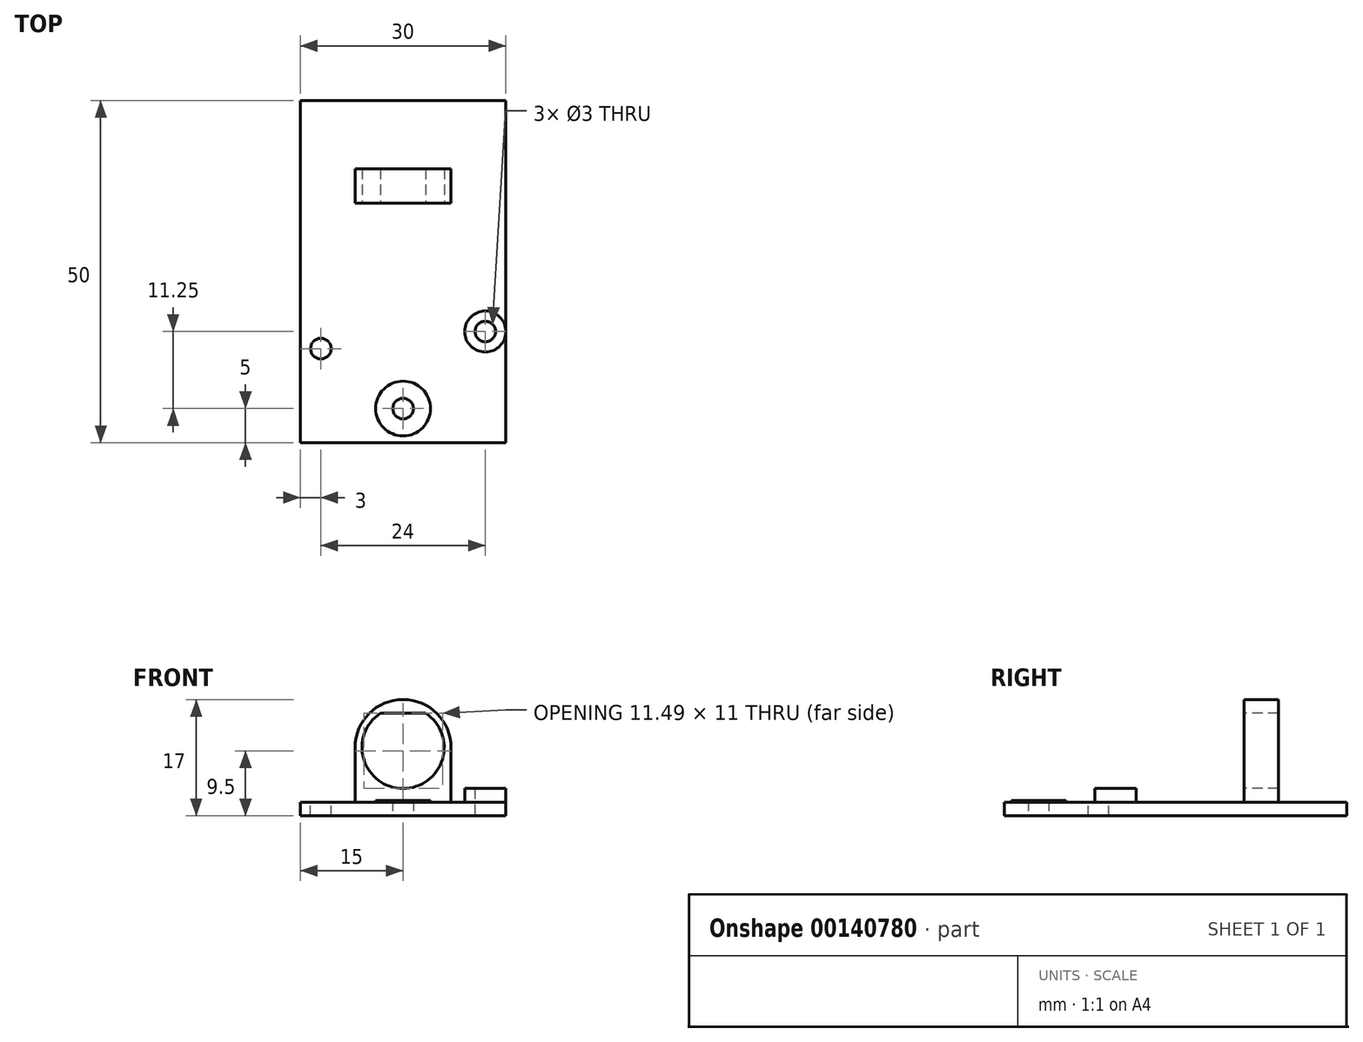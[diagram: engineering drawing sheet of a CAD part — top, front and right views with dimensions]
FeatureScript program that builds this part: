
annotation { "Feature Type Name" : "Feature", "Feature Type Description" : "" }
export const myFeature = defineFeature(function(context is Context, id is Id, definition is map)
    precondition{}
    {
        {
            var Q0;
            Q0=qCreatedBy(makeId("Front.planeOp"),FACE);
            var sketch = newSketch(context, id + "F0", { "sketchPlane" : qUnion([Q0])});
            skLineSegment(sketch, "E0.bottom", {"start": v(-3.32, 15) * mm, "end": v(3.32, 15) * mm});
            skArc(sketch, "E1", {"start": v(7, 10) * mm, "mid": v(0, 17) * mm, "end": v(-7, 10) * mm});
            skLineSegment(sketch, "E2", {"start": v(-7, 10) * mm, "end": v(-7, 2) * mm});
            skLineSegment(sketch, "E3", {"start": v(7, 10) * mm, "end": v(7, 2) * mm});
            skLineSegment(sketch, "E4", {"start": v(-7, 2) * mm, "end": v(-15, 2) * mm});
            skLineSegment(sketch, "E5", {"start": v(-15, 2) * mm, "end": v(-15, 0) * mm});
            skLineSegment(sketch, "E6", {"start": v(15, 0) * mm, "end": v(15, 2) * mm});
            skLineSegment(sketch, "E7", {"start": v(15, 2) * mm, "end": v(7, 2) * mm});
            skLineSegment(sketch, "E8", {"start": v(-15, 0) * mm, "end": v(15, 0) * mm});
            skArc(sketch, "E9", {"start": v(-3.32, 15) * mm, "mid": v(0, 4) * mm, "end": v(3.32, 15) * mm});
            skLineSegment(sketch, "E10", {"start": v(-7, 2) * mm, "end": v(7, 2) * mm});
            skSolve(sketch);
        }
        {
            var Q0;
            Q0=makeQuery(id+"F0.imprint","IMPRINT",FACE,{"disambiguationData":[TD([[makeQuery(id+"F0.imprint","IMPRINT",EDGE,{"derivedFrom":sQuery(id+"F0.wireOp",EDGE,"E0.bottom")}),1.0]])]});
            extrude(context, id + "F1", {"entities" : qUnion([Q0]), "oppositeDirection" : true, "depth" : 5 * mm});
        }
        {
            var Q0;
            {var subQ0=sQuery(id+"F0.wireOp",EDGE,"rBDJkf6V-3IXR-hIOR-VNlQ-4rZEFsfYJzs1");Q0=makeQuery(id+"F0.imprint","IMPRINT",FACE,{"disambiguationData":[TD([[makeQuery(id+"F0.imprint","IMPRINT",EDGE,{"derivedFrom":subQ0}),1.0]])]});}
            var Q1;
            {var subQ3=sQuery(id+"F0.wireOp",EDGE,"E4");Q1=makeQuery(id+"F0.imprint","IMPRINT",FACE,{"disambiguationData":[TD([[makeQuery(id+"F0.imprint","IMPRINT",EDGE,{"derivedFrom":subQ3}),1.0]])]});}
            extrude(context, id + "F2", {"entities" : qUnion([Q0, Q1]), "operationType" : NewBodyOperationType.ADD, "oppositeDirection" : true, "depth" : 15 * mm});
        }
        {
            var Q0;
            {var subQ0=sQuery(id+"F0.wireOp",EDGE,"rBDJkf6V-3IXR-hIOR-VNlQ-4rZEFsfYJzs1");Q0=makeQuery(id+"F0.imprint","IMPRINT",FACE,{"disambiguationData":[TD([[makeQuery(id+"F0.imprint","IMPRINT",EDGE,{"derivedFrom":subQ0}),1.0]])]});}
            var Q1;
            {var subQ3=sQuery(id+"F0.wireOp",EDGE,"E4");Q1=makeQuery(id+"F0.imprint","IMPRINT",FACE,{"disambiguationData":[TD([[makeQuery(id+"F0.imprint","IMPRINT",EDGE,{"derivedFrom":subQ3}),1.0]])]});}
            extrude(context, id + "F3", {"entities" : qUnion([Q0, Q1]), "operationType" : NewBodyOperationType.ADD, "depth" : 35 * mm});
        }
        {
            var Q0;
            {var subQ0=sQuery(id+"F0.wireOp",EDGE,"9Bnnmyrw-iAOv-QSIy-XyIa-5J96ybDtpeLF");var subQ1=sQuery(id+"F0.wireOp",EDGE,"OCGj93Nr-ASNq-xmZx-sLMK-JFpCvM9ZKUq5");var subQ2=sQuery(id+"F0.wireOp",EDGE,"E7");var subQ3=sQuery(id+"F0.wireOp",EDGE,"E4");var subQ4=sQuery(id+"F0.wireOp",EDGE,"E0.top");Q0=makeQuery(id+"F3.boolean.opBoolean","MERGE",FACE,{"derivedFrom":[makeQuery(id+"F2.opExtrude","SWEPT_FACE",FACE,{"disambiguationData":[OSD([subQ4,subQ3,subQ2,subQ1,subQ0])]}),makeQuery(id+"F3.opExtrude","SWEPT_FACE",FACE,{"disambiguationData":[OSD([subQ4,subQ3,subQ2,subQ1,subQ0])]})]});}
            var sketch = newSketch(context, id + "F4", { "sketchPlane" : qUnion([Q0])});
            skCircle(sketch, "E11", {"center": v(-12, -21.25) * mm, "radius": 1.5 * mm});
            skCircle(sketch, "E12", {"center": v(12, -18.75) * mm, "radius": 1.5 * mm});
            skCircle(sketch, "E13", {"center": v(0, -30) * mm, "radius": 1.5 * mm});
            skCircle(sketch, "E14", {"center": v(12, -18.75) * mm, "radius": 3 * mm});
            skCircle(sketch, "E15", {"center": v(0, -30) * mm, "radius": 4 * mm});
            skSolve(sketch);
        }
        {
            var Q0;
            Q0=makeQuery(id+"F4.imprint","IMPRINT",FACE,{"disambiguationData":[TD([[makeQuery(id+"F4.imprint","IMPRINT",EDGE,{"derivedFrom":sQuery(id+"F4.wireOp",EDGE,"E12")}),-1.0]])]});
            extrude(context, id + "F5", {"entities" : qUnion([Q0]), "operationType" : NewBodyOperationType.ADD, "depth" : 2 * mm});
        }
        {
            var Q0;
            Q0=makeQuery(id+"F4.imprint","IMPRINT",FACE,{"disambiguationData":[TD([[makeQuery(id+"F4.imprint","IMPRINT",EDGE,{"derivedFrom":sQuery(id+"F4.wireOp",EDGE,"E13")}),-1.0]])]});
            extrude(context, id + "F6", {"entities" : qUnion([Q0]), "operationType" : NewBodyOperationType.ADD, "depth" : .25 * mm});
        }
        {
            var Q0;
            Q0=makeQuery(id+"F4.imprint","IMPRINT",FACE,{"disambiguationData":[TD([[makeQuery(id+"F4.imprint","IMPRINT",EDGE,{"derivedFrom":sQuery(id+"F4.wireOp",EDGE,"E11")}),1.0]])]});
            var Q1;
            Q1=makeQuery(id+"F4.imprint","IMPRINT",FACE,{"disambiguationData":[TD([[makeQuery(id+"F4.imprint","IMPRINT",EDGE,{"derivedFrom":sQuery(id+"F4.wireOp",EDGE,"E13")}),1.0]])]});
            var Q2;
            Q2=makeQuery(id+"F4.imprint","IMPRINT",FACE,{"disambiguationData":[TD([[makeQuery(id+"F4.imprint","IMPRINT",EDGE,{"derivedFrom":sQuery(id+"F4.wireOp",EDGE,"E12")}),1.0]])]});
            extrude(context, id + "F7", {"entities" : qUnion([Q0, Q1, Q2]), "operationType" : NewBodyOperationType.REMOVE, "oppositeDirection" : true, "depth" : 25 * mm});
        }
    });
